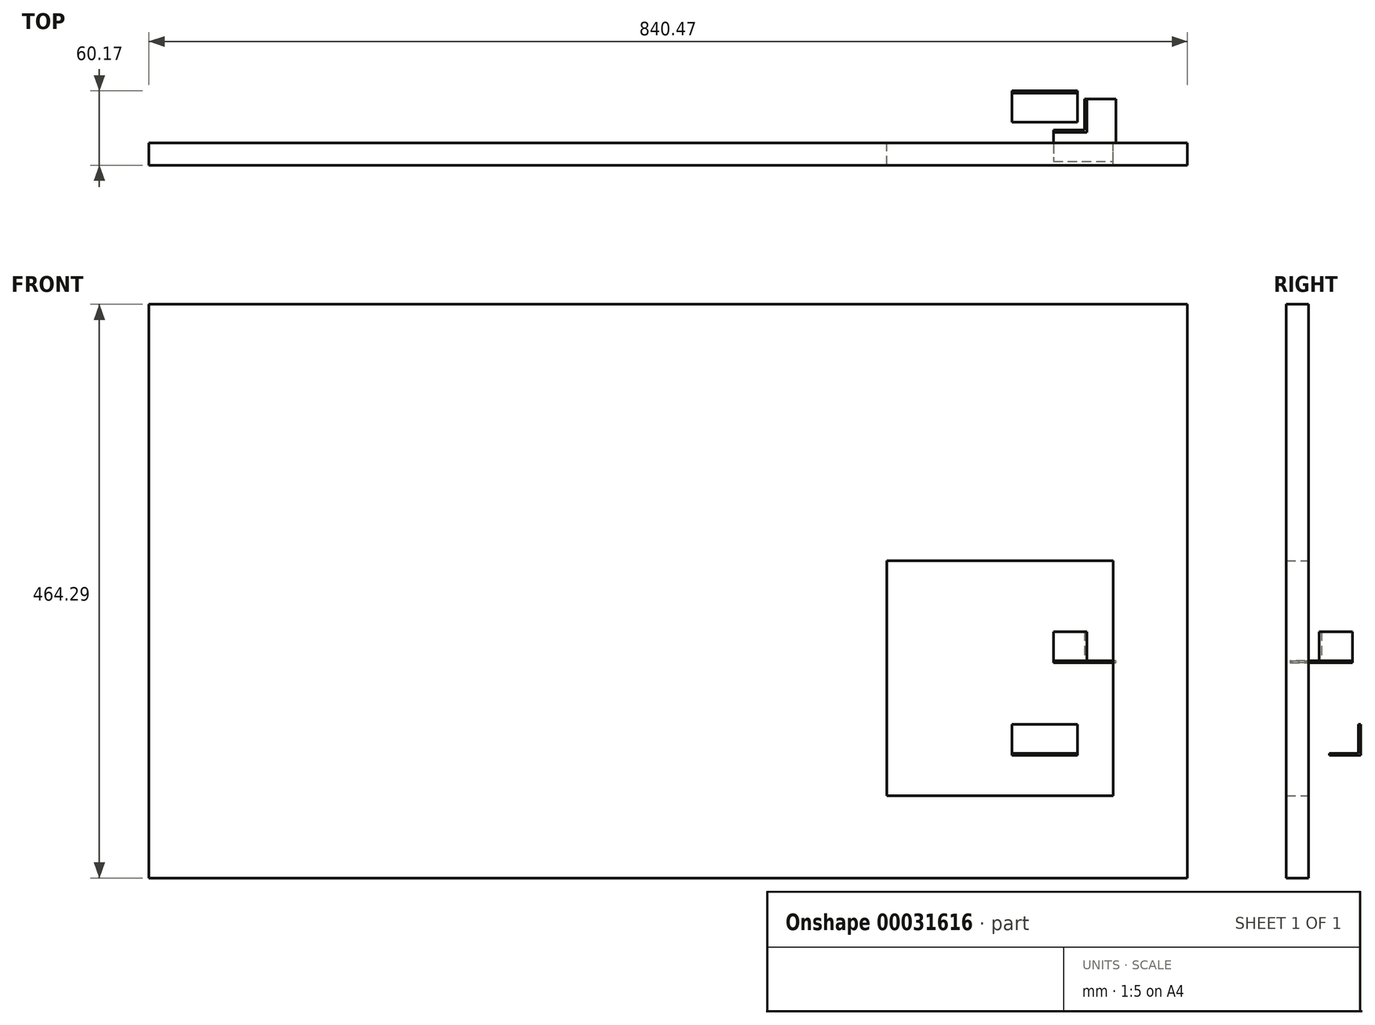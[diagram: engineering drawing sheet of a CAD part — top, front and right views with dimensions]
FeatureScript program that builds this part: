
annotation { "Feature Type Name" : "Feature", "Feature Type Description" : "" }
export const myFeature = defineFeature(function(context is Context, id is Id, definition is map)
    precondition{}
    {
        {
            assignVariable(context, id + "F0", {"name" : "AngleWidth", "anyValue" : 25.25});
        }
        {
            assignVariable(context, id + "F1", {"name" : "AngleThickness", "anyValue" : 1.7});
        }
        {
            var Q0;
            Q0=qCreatedBy(makeId("Top.planeOp"),FACE);
            var sketch = newSketch(context, id + "F2", { "sketchPlane" : qUnion([Q0])});
            skLineSegment(sketch, "E0.bottom", {"start": v(-60.08, 42.17) * mm, "end": v(-7.05, 42.17) * mm});
            skLineSegment(sketch, "E0.top", {"start": v(-60.08, 16.92) * mm, "end": v(-7.05, 16.92) * mm});
            skLineSegment(sketch, "E0.left", {"start": v(-60.08, 42.17) * mm, "end": v(-60.08, 16.92) * mm});
            skLineSegment(sketch, "E0.right", {"start": v(-7.05, 42.17) * mm, "end": v(-7.05, 16.92) * mm});
            skLineSegment(sketch, "E1", {"start": v(-60.08, 40.47) * mm, "end": v(-7.05, 40.47) * mm});
            skSolve(sketch);
        }
        {
            var Q0;
            {var subQ0=sQuery(id+"F2.wireOp",EDGE,"E0.top");Q0=makeQuery(id+"F2.imprint","IMPRINT",FACE,{"disambiguationData":[TD([[makeQuery(id+"F2.imprint","IMPRINT",EDGE,{"derivedFrom":subQ0}),1.0]])]});}
            extrude(context, id + "F3", {"entities" : qUnion([Q0]), "depth" : (getVariable(context, 'AngleThickness')) * mm});
        }
        {
            var Q0;
            {var subQ0=sQuery(id+"F2.wireOp",EDGE,"E0.bottom");Q0=makeQuery(id+"F2.imprint","IMPRINT",FACE,{"disambiguationData":[TD([[makeQuery(id+"F2.imprint","IMPRINT",EDGE,{"derivedFrom":subQ0}),-1.0]])]});}
            extrude(context, id + "F4", {"entities" : qUnion([Q0]), "operationType" : NewBodyOperationType.ADD, "depth" : (getVariable(context, 'AngleWidth')) * mm});
        }
        {
            var Q0;
            Q0=qCreatedBy(makeId("Front.planeOp"),FACE);
            var sketch = newSketch(context, id + "F5", { "sketchPlane" : qUnion([Q0])});
            skLineSegment(sketch, "E2.bottom", {"start": v(81.87, -99.12) * mm, "end": v(-758.6, -99.12) * mm});
            skLineSegment(sketch, "E2.top", {"start": v(81.87, 365.17) * mm, "end": v(-758.6, 365.17) * mm});
            skLineSegment(sketch, "E2.left", {"start": v(81.87, -99.12) * mm, "end": v(81.87, 365.17) * mm});
            skLineSegment(sketch, "E2.right", {"start": v(-758.6, -99.12) * mm, "end": v(-758.6, 365.17) * mm});
            skLineSegment(sketch, "E3.bottom", {"start": v(21.87, -32.5) * mm, "end": v(-161.44, -32.5) * mm});
            skLineSegment(sketch, "E3.top", {"start": v(21.87, 157.76) * mm, "end": v(-161.44, 157.76) * mm});
            skLineSegment(sketch, "E3.left", {"start": v(21.87, -32.5) * mm, "end": v(21.87, 157.76) * mm});
            skLineSegment(sketch, "E3.right", {"start": v(-161.44, -32.5) * mm, "end": v(-161.44, 157.76) * mm});
            skSolve(sketch);
        }
        {
            var Q0;
            Q0=makeQuery(id+"F5.imprint","IMPRINT",FACE,{"disambiguationData":[TD([[makeQuery(id+"F5.imprint","IMPRINT",EDGE,{"derivedFrom":sQuery(id+"F5.wireOp",EDGE,"E2.bottom")}),-1.0]])]});
            extrude(context, id + "F6", {"entities" : qUnion([Q0]), "depth" : 18 * mm});
        }
        {
            var Q0;
            Q0=qCreatedBy(makeId("Top.planeOp"),FACE);
            cPlane(context, id + "F7", {"entities" : qUnion([Q0]), "cplaneType" : CPlaneType.OFFSET, "offset" : 75 * mm, "width" : 150 * mm, "height" : 150 * mm});
        }
        {
            var Q0;
            Q0=qCreatedBy(id+"F7.planeOp",FACE);
            var sketch = newSketch(context, id + "F8", { "sketchPlane" : qUnion([Q0])});
            skLineSegment(sketch, "E4.bottom", {"start": v(-26.51, 10.44) * mm, "end": v(-1.26, 10.44) * mm});
            skLineSegment(sketch, "E4.top", {"start": v(-26.51, -14.8) * mm, "end": v(-1.26, -14.8) * mm});
            skLineSegment(sketch, "E4.left", {"start": v(-26.51, 10.44) * mm, "end": v(-26.51, -14.8) * mm});
            skLineSegment(sketch, "E4.right", {"start": v(-1.26, 35.7) * mm, "end": v(-1.26, -14.8) * mm});
            skLineSegment(sketch, "E5", {"start": v(-26.51, 8.74) * mm, "end": v(-1.26, 8.74) * mm});
            skLineSegment(sketch, "E6", {"start": v(-1.26, -14.8) * mm, "end": v(23.99, -14.8) * mm});
            skLineSegment(sketch, "E7", {"start": v(-1.26, 35.7) * mm, "end": v(23.99, 35.7) * mm});
            skLineSegment(sketch, "E8", {"start": v(23.99, 35.7) * mm, "end": v(23.99, -14.8) * mm});
            skLineSegment(sketch, "E9", {"start": v(0.44, 35.7) * mm, "end": v(0.44, -14.8) * mm});
            skLineSegment(sketch, "E10", {"start": v(-1.26, 10.44) * mm, "end": v(0.44, 10.44) * mm});
            skLineSegment(sketch, "E11", {"start": v(-1.26, 8.74) * mm, "end": v(0.44, 8.74) * mm});
            skSolve(sketch);
        }
        {
            var Q0;
            {var subQ0=sQuery(id+"F8.wireOp",EDGE,"E4.bottom");Q0=makeQuery(id+"F8.imprint","IMPRINT",FACE,{"disambiguationData":[TD([[makeQuery(id+"F8.imprint","IMPRINT",EDGE,{"derivedFrom":subQ0}),-1.0]])]});}
            var Q1;
            {var subQ0=sQuery(id+"F8.wireOp",EDGE,"E10");Q1=makeQuery(id+"F8.imprint","IMPRINT",FACE,{"disambiguationData":[TD([[makeQuery(id+"F8.imprint","IMPRINT",EDGE,{"derivedFrom":subQ0}),-1.0]])]});}
            var Q2;
            {var subQ0=sQuery(id+"F8.wireOp",EDGE,"E10");Q2=makeQuery(id+"F8.imprint","IMPRINT",FACE,{"disambiguationData":[TD([[makeQuery(id+"F8.imprint","IMPRINT",EDGE,{"derivedFrom":subQ0}),1.0]])]});}
            extrude(context, id + "F9", {"entities" : qUnion([Q0, Q1, Q2]), "depth" : (getVariable(context, 'AngleWidth')) * mm});
        }
        {
            var Q0;
            {var subQ0=sQuery(id+"F8.wireOp",EDGE,"E4.top");Q0=makeQuery(id+"F8.imprint","IMPRINT",FACE,{"disambiguationData":[TD([[makeQuery(id+"F8.imprint","IMPRINT",EDGE,{"derivedFrom":subQ0}),1.0]])]});}
            var Q1;
            {var subQ3=sQuery(id+"F8.wireOp",EDGE,"E11");Q1=makeQuery(id+"F8.imprint","IMPRINT",FACE,{"disambiguationData":[TD([[makeQuery(id+"F8.imprint","IMPRINT",EDGE,{"derivedFrom":subQ3}),-1.0]])]});}
            var Q2;
            {var subQ4=sQuery(id+"F8.wireOp",EDGE,"E8");Q2=makeQuery(id+"F8.imprint","IMPRINT",FACE,{"disambiguationData":[TD([[makeQuery(id+"F8.imprint","IMPRINT",EDGE,{"derivedFrom":subQ4}),-1.0]])]});}
            extrude(context, id + "F10", {"entities" : qUnion([Q0, Q1, Q2]), "operationType" : NewBodyOperationType.ADD, "depth" : (getVariable(context, 'AngleThickness')) * mm});
        }
    });
